# Revit family: Toilet-Floor_Mount_Hidden_Cord-KOHLER-Spacity-K-28020MY_1
name_source: partatom
category: Plumbing Fixtures
units: mm (PartAtom-declared; Revit-internal decimal feet)

## family parameters
Cut with Voids When Loaded = No
Host = Face
Maintain Annotation Orientation = No
OmniClass Number = 23.31.19.00
OmniClass Title = Toilets
Part Type = Normal
Room Calculation Point = No
Round Connector Dimension = Use Diameter
Shared = No

## types (1)
- 0-White
    ADA Compliant = No
    Apparent Load = 2200 VA
    Assembly Code = D2010100
    CW Connection = Yes
    Cold Water Inlet = Cold Water Inlet
    Cold Water Inlet Seat = Cold Water Inlet Seat
    Date Modified = 12/23/2022
    Default Elevation = 0"
    Description = One Piece 305mm Toilet - Hidden Cord
    Electrical Connection = Yes
    Electrical Note = One Dedicated Circuit Required
    Finish = Kohler-Vitreous_China-0-White
    Flow Rate = 0 GPM
    Flush Rate- GPF = 1.0 GPF
    Flush Rate- LPF = 4.0 LPF
    Frequency = 50 Hz
    HW Connection = No
    Height = 27 3/8"
    Hot Water Inlet = Hot Water Inlet
    Length = 26 3/4"
    Manufacturer = Kohler Co.
    Master Format 2014 = 22 42 13.13
    Master Format 2014 Name = Residential Water Closets
    Material = Vitreous China
    Model = K-28020MY-HC-0
    Pressure = 0.00 psi
    Product Name = Spacity
    Rough-In = 12"
    Seat Included = No
    Type = 1
    URL = https://www.kohler.my
    Vent Connection = No
    Voltage = 220 V
    Waste Connection = Yes
    Waste Water Outlet = Waste Water Outlet
    WaterSense Certified = No
    Width = 17 5/8"

## geometry (parser evidence)
native form markers: Sweep x4
no freeform markers — native parametric forms only
